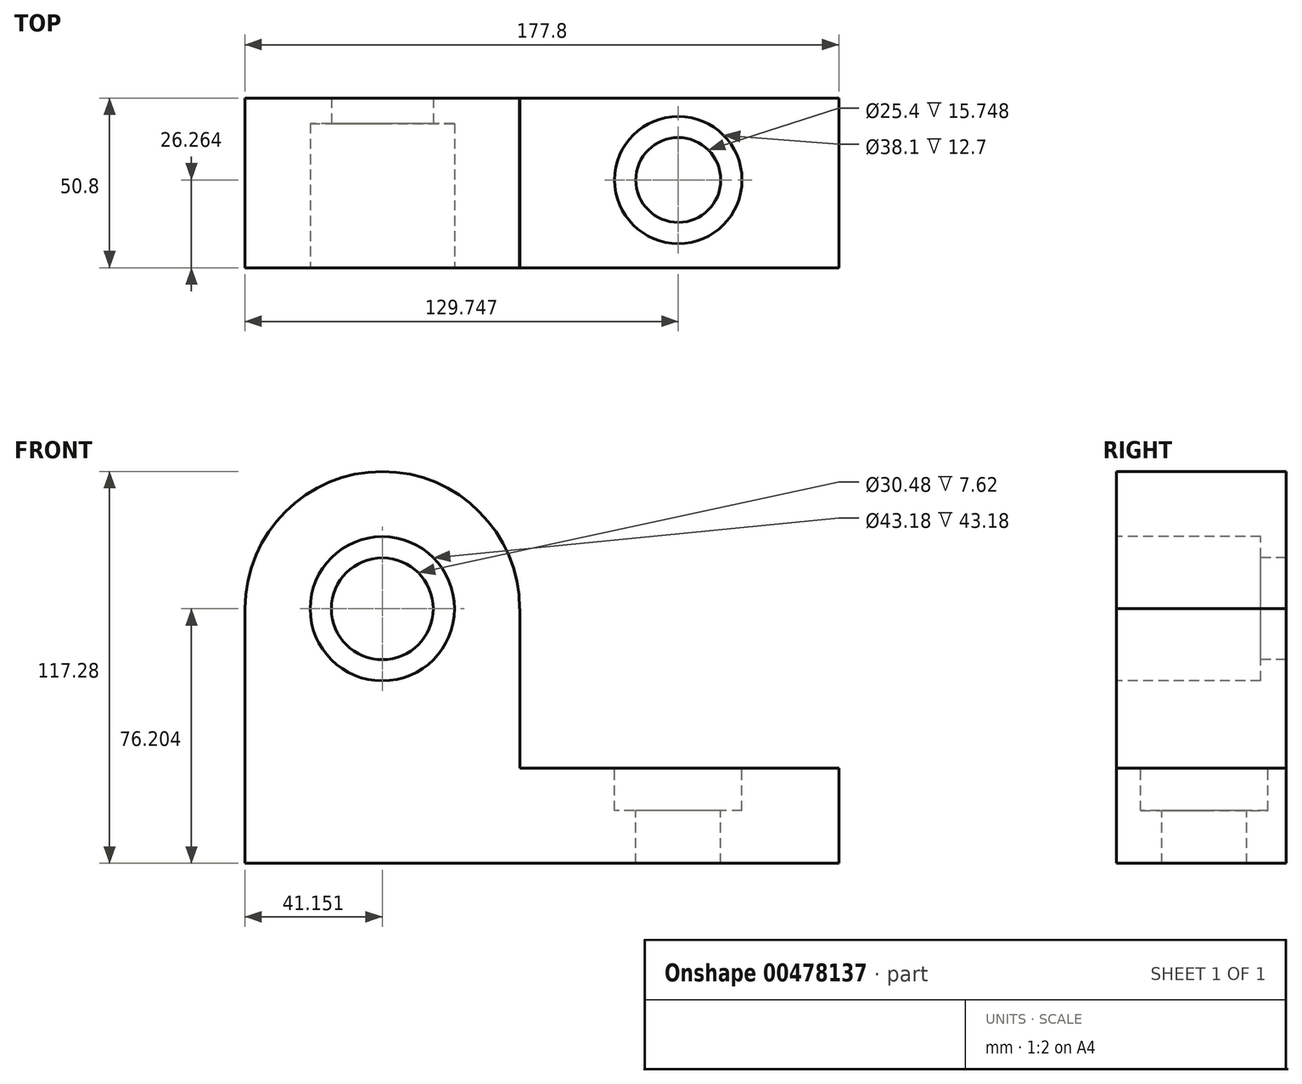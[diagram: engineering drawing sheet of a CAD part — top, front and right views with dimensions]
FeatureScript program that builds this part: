
annotation { "Feature Type Name" : "Feature", "Feature Type Description" : "" }
export const myFeature = defineFeature(function(context is Context, id is Id, definition is map)
    precondition{}
    {
        {
            var Q0;
            Q0=qCreatedBy(makeId("Front.planeOp"),FACE);
            var sketch = newSketch(context, id + "F0", { "sketchPlane" : qUnion([Q0])});
            skLineSegment(sketch, "E0", {"start": v(-88.29, -25.76) * mm, "end": v(89.51, -25.76) * mm});
            skLineSegment(sketch, "E1", {"start": v(89.51, -25.76) * mm, "end": v(89.51, 2.7) * mm});
            skLineSegment(sketch, "E2", {"start": v(-88.29, -25.76) * mm, "end": v(-88.29, 50.44) * mm});
            skLineSegment(sketch, "E3", {"start": v(-88.29, 50.44) * mm, "end": v(-47.14, 50.44) * mm});
            skLineSegment(sketch, "E4", {"start": v(-47.14, 50.44) * mm, "end": v(-6, 50.44) * mm});
            skCircle(sketch, "E5", {"center": v(-47.14, 50.44) * mm, "radius": 41.08 * mm});
            skLineSegment(sketch, "E6", {"start": v(89.51, 2.7) * mm, "end": v(-6, 2.7) * mm});
            skLineSegment(sketch, "E7", {"start": v(-6, 2.7) * mm, "end": v(-6, 50.44) * mm});
            skCircle(sketch, "E8", {"center": v(-47.14, 50.44) * mm, "radius": 21.84 * mm});
            skSolve(sketch);
        }
        {
            var Q0;
            {var subQ0=sQuery(id+"F0.wireOp",EDGE,"E5");var subQ1=sQuery(id+"F0.wireOp",EDGE,"E3");var subQ2=makeQuery(id+"F0.imprint","INTERSECT",VERTEX,{"derivedFrom":[subQ1,subQ0]});Q0=makeQuery(id+"F0.imprint","IMPRINT",FACE,{"disambiguationData":[TD([[makeQuery(id+"F0.imprint","IMPRINT",EDGE,{"disambiguationData":[TD([[subQ2,-1.0]])],"derivedFrom":subQ1}),1.0]])]});}
            var Q1;
            {var subQ0=sQuery(id+"F0.wireOp",EDGE,"E5");var subQ1=sQuery(id+"F0.wireOp",EDGE,"E3");var subQ2=makeQuery(id+"F0.imprint","INTERSECT",VERTEX,{"derivedFrom":[subQ1,subQ0]});Q1=makeQuery(id+"F0.imprint","IMPRINT",FACE,{"disambiguationData":[TD([[makeQuery(id+"F0.imprint","IMPRINT",EDGE,{"disambiguationData":[TD([[subQ2,-1.0]])],"derivedFrom":subQ1}),-1.0]])]});}
            var Q2;
            Q2=makeQuery(id+"F0.imprint","IMPRINT",FACE,{"disambiguationData":[TD([[makeQuery(id+"F0.imprint","IMPRINT",EDGE,{"derivedFrom":sQuery(id+"F0.wireOp",EDGE,"E0")}),1.0]])]});
            extrude(context, id + "F1", {"entities" : qUnion([Q0, Q1, Q2]), "depth" : 25.4 * mm});
        }
        {
            var Q0;
            Q0=makeQuery(id+"F1.opExtrude","CAP_FACE",FACE,{"disambiguationData":[OSD([sQuery(id+"F0.wireOp",EDGE,"E0"),sQuery(id+"F0.wireOp",EDGE,"E1"),sQuery(id+"F0.wireOp",EDGE,"E2"),sQuery(id+"F0.wireOp",EDGE,"E3"),sQuery(id+"F0.wireOp",EDGE,"E4"),sQuery(id+"F0.wireOp",EDGE,"E5"),sQuery(id+"F0.wireOp",EDGE,"E6"),sQuery(id+"F0.wireOp",EDGE,"E7"),sQuery(id+"F0.wireOp",EDGE,"E8")])],"isStart":false});
            extrude(context, id + "F2", {"entities" : qUnion([Q0]), "operationType" : NewBodyOperationType.ADD, "depth" : 25.4 * mm});
        }
        {
            var Q0;
            {var subQ0=sQuery(id+"F0.wireOp",EDGE,"E6");Q0=makeQuery(id+"F2.boolean.opBoolean","MERGE",FACE,{"derivedFrom":[makeQuery(id+"F1.opExtrude","SWEPT_FACE",FACE,{"disambiguationData":[OSD([subQ0])]}),makeQuery(id+"F2.opExtrude","SWEPT_FACE",FACE,{"disambiguationData":[OSD([subQ0])]})]});}
            var sketch = newSketch(context, id + "F3", { "sketchPlane" : qUnion([Q0])});
            skCircle(sketch, "E9", {"center": v(41.46, -24.54) * mm, "radius": 14.95 * mm});
            skSolve(sketch);
        }
        {
            var Q0;
            Q0=sQuery(id+"F3.wireOp",VERTEX,"E9.center");
            var Q1;
            Q1=makeQuery(id+"F1.opExtrude","SWEPT_BODY",BODY,{"disambiguationData":[OSD([sQuery(id+"F0.wireOp",EDGE,"E0"),sQuery(id+"F0.wireOp",EDGE,"E1"),sQuery(id+"F0.wireOp",EDGE,"E2"),sQuery(id+"F0.wireOp",EDGE,"E3"),sQuery(id+"F0.wireOp",EDGE,"E4"),sQuery(id+"F0.wireOp",EDGE,"E5"),sQuery(id+"F0.wireOp",EDGE,"E6"),sQuery(id+"F0.wireOp",EDGE,"E7"),sQuery(id+"F0.wireOp",EDGE,"E8")])]});
            hole(context, id + "F4", {"style" : HoleStyle.C_BORE, "endStyle" : HoleEndStyle.THROUGH, "holeDiameter" : 25.4 * mm, "cBoreDiameter" : 38.1 * mm, "cBoreDepth" : 12.7 * mm, "isTappedThrough" : true, "tappedDepth" : 12.7 * mm, "tapClearance" : 3, "locations" : qUnion([Q0]), "scope" : qUnion([Q1])});
        }
        {
            var Q0;
            {var subQ0=sQuery(id+"F0.wireOp",EDGE,"E4");var subQ1=sQuery(id+"F0.wireOp",EDGE,"E3");var subQ2=makeQuery(id+"F0.imprint","INTERSECT",VERTEX,{"derivedFrom":[subQ1,subQ0]});Q0=makeQuery(id+"F0.imprint","IMPRINT",FACE,{"disambiguationData":[TD([[makeQuery(id+"F0.imprint","IMPRINT",EDGE,{"disambiguationData":[TD([[subQ2,1.0]])],"derivedFrom":subQ1}),-1.0]])]});}
            var Q1;
            {var subQ0=sQuery(id+"F0.wireOp",EDGE,"E4");var subQ1=sQuery(id+"F0.wireOp",EDGE,"E3");var subQ2=makeQuery(id+"F0.imprint","INTERSECT",VERTEX,{"derivedFrom":[subQ1,subQ0]});Q1=makeQuery(id+"F0.imprint","IMPRINT",FACE,{"disambiguationData":[TD([[makeQuery(id+"F0.imprint","IMPRINT",EDGE,{"disambiguationData":[TD([[subQ2,1.0]])],"derivedFrom":subQ1}),1.0]])]});}
            extrude(context, id + "F5", {"entities" : qUnion([Q0, Q1]), "operationType" : NewBodyOperationType.ADD, "depth" : 25.4 * mm});
        }
        {
            var Q0;
            Q0=makeQuery(id+"F5.opExtrude","CAP_FACE",FACE,{"disambiguationData":[OSD([sQuery(id+"F0.wireOp",EDGE,"E8")])],"isStart":false});
            extrude(context, id + "F6", {"entities" : qUnion([Q0]), "operationType" : NewBodyOperationType.ADD, "depth" : 25.4 * mm});
        }
        {
            var Q0;
            {var subQ0=sQuery(id+"F0.wireOp",EDGE,"E8");Q0=makeQuery(id+"F6.boolean.opBoolean","MERGE",FACE,{"derivedFrom":[makeQuery(id+"F2.opExtrude","CAP_FACE",FACE,{"disambiguationData":[OSD([sQuery(id+"F0.wireOp",EDGE,"E0"),sQuery(id+"F0.wireOp",EDGE,"E1"),sQuery(id+"F0.wireOp",EDGE,"E2"),sQuery(id+"F0.wireOp",EDGE,"E3"),sQuery(id+"F0.wireOp",EDGE,"E4"),sQuery(id+"F0.wireOp",EDGE,"E5"),sQuery(id+"F0.wireOp",EDGE,"E6"),sQuery(id+"F0.wireOp",EDGE,"E7"),subQ0])],"isStart":false}),makeQuery(id+"F6.opExtrude","CAP_FACE",FACE,{"disambiguationData":[OSD([subQ0])],"isStart":false})]});}
            var sketch = newSketch(context, id + "F7", { "sketchPlane" : qUnion([Q0])});
            skCircle(sketch, "E10", {"center": v(-47.14, 50.44) * mm, "radius": 25.04 * mm});
            skSolve(sketch);
        }
        {
            var Q0;
            Q0=sQuery(id+"F7.wireOp",VERTEX,"E10.center");
            var Q1;
            Q1=makeQuery(id+"F1.opExtrude","SWEPT_BODY",BODY,{"disambiguationData":[OSD([sQuery(id+"F0.wireOp",EDGE,"E0"),sQuery(id+"F0.wireOp",EDGE,"E1"),sQuery(id+"F0.wireOp",EDGE,"E2"),sQuery(id+"F0.wireOp",EDGE,"E3"),sQuery(id+"F0.wireOp",EDGE,"E4"),sQuery(id+"F0.wireOp",EDGE,"E5"),sQuery(id+"F0.wireOp",EDGE,"E6"),sQuery(id+"F0.wireOp",EDGE,"E7"),sQuery(id+"F0.wireOp",EDGE,"E8")])]});
            hole(context, id + "F8", {"style" : HoleStyle.C_BORE, "endStyle" : HoleEndStyle.THROUGH, "holeDiameter" : 30.48 * mm, "cBoreDiameter" : 43.18 * mm, "cBoreDepth" : 43.18 * mm, "isTappedThrough" : true, "tappedDepth" : 12.7 * mm, "tapClearance" : 3, "locations" : qUnion([Q0]), "scope" : qUnion([Q1])});
        }
    });
